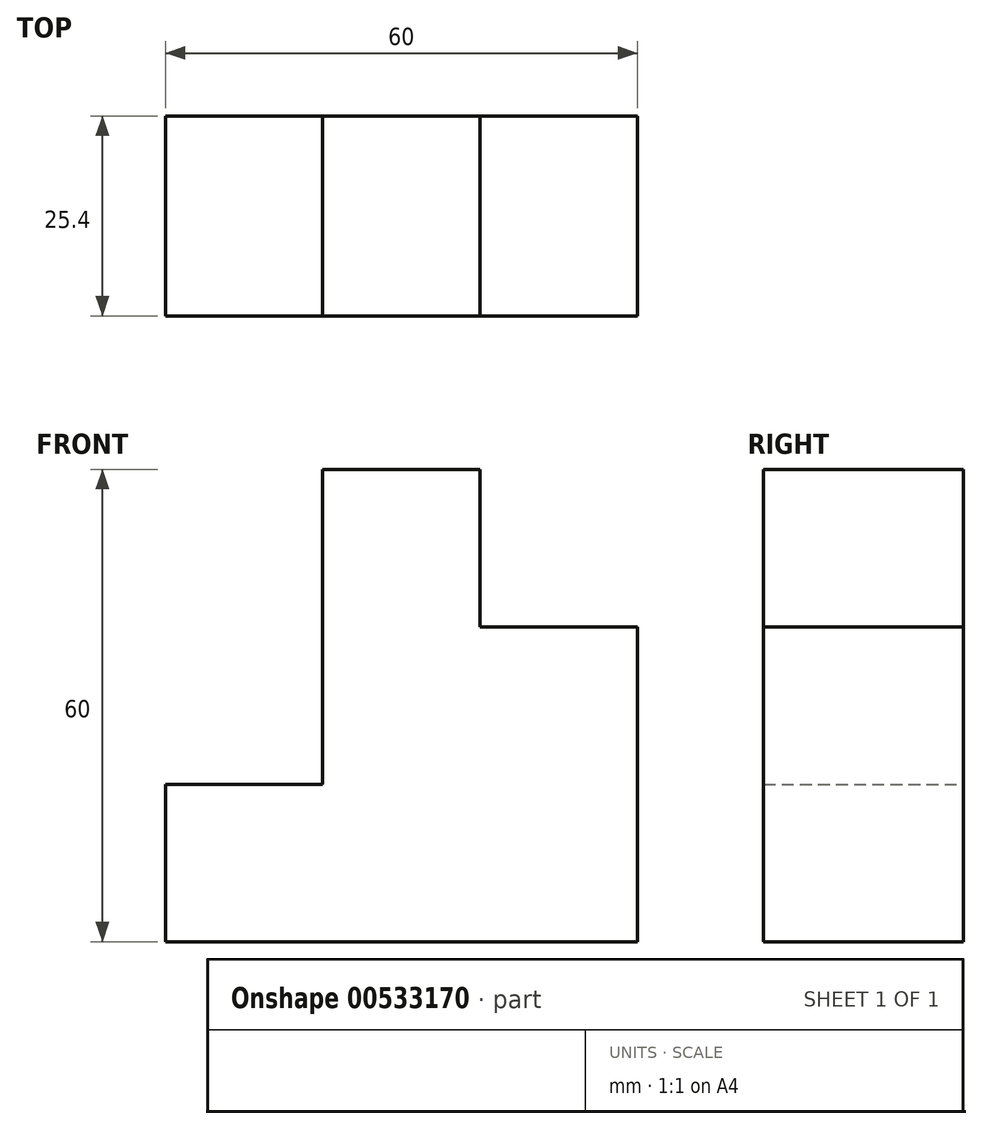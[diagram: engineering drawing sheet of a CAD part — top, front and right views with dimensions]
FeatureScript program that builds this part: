
annotation { "Feature Type Name" : "Feature", "Feature Type Description" : "" }
export const myFeature = defineFeature(function(context is Context, id is Id, definition is map)
    precondition{}
    {
        {
            var Q0;
            Q0=qCreatedBy(makeId("Front.planeOp"),FACE);
            var sketch = newSketch(context, id + "F0", { "sketchPlane" : qUnion([Q0])});
            skLineSegment(sketch, "E0.bottom", {"start": v(-10.22, 18.25) * mm, "end": v(29.78, 18.25) * mm});
            skLineSegment(sketch, "E0.top", {"start": v(-10.22, -21.75) * mm, "end": v(29.78, -21.75) * mm});
            skLineSegment(sketch, "E0.left", {"start": v(-10.22, 18.25) * mm, "end": v(-10.22, -21.75) * mm});
            skLineSegment(sketch, "E0.right", {"start": v(29.78, 18.25) * mm, "end": v(29.78, -21.75) * mm});
            skLineSegment(sketch, "E1.bottom", {"start": v(-10.22, 38.25) * mm, "end": v(9.78, 38.25) * mm});
            skLineSegment(sketch, "E1.top", {"start": v(-10.22, 18.25) * mm, "end": v(9.78, 18.25) * mm});
            skLineSegment(sketch, "E1.left", {"start": v(-10.22, 38.25) * mm, "end": v(-10.22, 18.25) * mm});
            skLineSegment(sketch, "E1.right", {"start": v(9.78, 38.25) * mm, "end": v(9.78, 18.25) * mm});
            skLineSegment(sketch, "E2.bottom", {"start": v(-30.22, -1.75) * mm, "end": v(-10.22, -1.75) * mm});
            skLineSegment(sketch, "E2.top", {"start": v(-30.22, -21.75) * mm, "end": v(-10.22, -21.75) * mm});
            skLineSegment(sketch, "E2.left", {"start": v(-30.22, -1.75) * mm, "end": v(-30.22, -21.75) * mm});
            skLineSegment(sketch, "E2.right", {"start": v(-10.22, -1.75) * mm, "end": v(-10.22, -21.75) * mm});
            skSolve(sketch);
        }
        {
            var Q0;
            Q0 = qSketchRegion(id + "F0", true);
            extrude(context, id + "F1", {"entities" : qUnion([Q0]), "depth" : 25.4 * mm, "offsetDistance" : 25.4 * mm});
        }
    });
